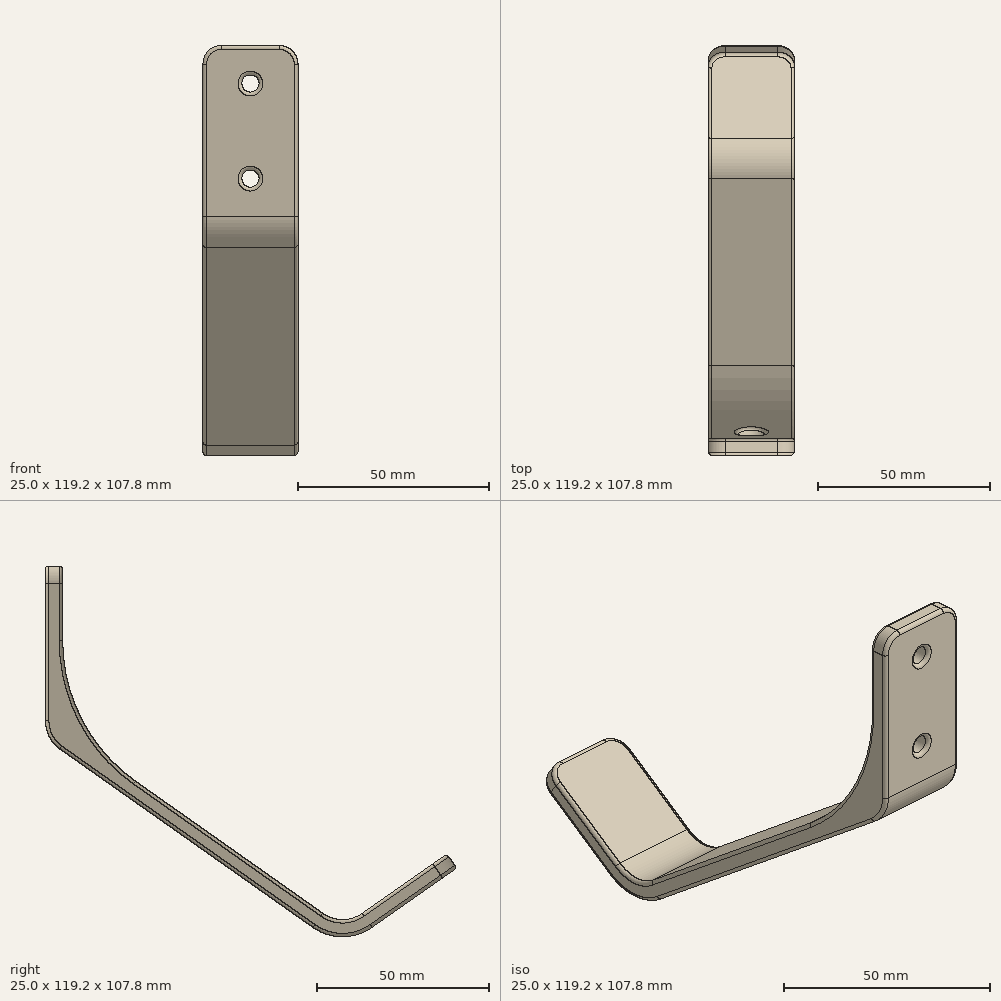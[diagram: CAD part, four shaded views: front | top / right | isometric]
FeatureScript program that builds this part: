
annotation { "Feature Type Name" : "Feature", "Feature Type Description" : "" }
export const myFeature = defineFeature(function(context is Context, id is Id, definition is map)
    precondition{}
    {
        {
            var Q0;
            Q0=qCreatedBy(makeId("Right.planeOp"),FACE);
            var sketch = newSketch(context, id + "F0", { "sketchPlane" : qUnion([Q0])});
            skLineSegment(sketch, "E0", {"start": v(0, 105) * mm, "end": v(0, 60) * mm});
            skLineSegment(sketch, "E1", {"start": v(2.12, 55.91) * mm, "end": v(75.67, 4.05) * mm});
            skLineSegment(sketch, "E2", {"start": v(87.17, 4.03) * mm, "end": v(111.74, 21.24) * mm});
            skPoint(sketch, "E3.visualSharp", {"position": v(81.41, 0) * mm});
            skArc(sketch, "E3.filletArc", {"start": v(75.67, 4.05) * mm, "mid": v(81.42, 2.22) * mm, "end": v(87.17, 4.03) * mm});
            skPoint(sketch, "E4.visualSharp", {"position": v(0, 57.4) * mm});
            skArc(sketch, "E4.filletArc", {"start": v(0, 60) * mm, "mid": v(0.56, 57.7) * mm, "end": v(2.12, 55.91) * mm});
            skLineSegment(sketch, "E5.0", {"start": v(90.04, -0.07) * mm, "end": v(114.61, 17.14) * mm});
            skLineSegment(sketch, "E5.1", {"start": v(-5, 105) * mm, "end": v(-5, 60) * mm});
            skArc(sketch, "E5.2", {"start": v(-5, 60) * mm, "mid": v(-3.88, 55.4) * mm, "end": v(-0.76, 51.83) * mm});
            skLineSegment(sketch, "E5.3", {"start": v(-0.76, 51.83) * mm, "end": v(72.8, -0.04) * mm});
            skArc(sketch, "E5.4", {"start": v(72.8, -0.04) * mm, "mid": v(81.4, -2.78) * mm, "end": v(90.04, -0.07) * mm});
            skLineSegment(sketch, "E6", {"start": v(0, 105) * mm, "end": v(-5, 105) * mm});
            skLineSegment(sketch, "E7", {"start": v(111.74, 21.24) * mm, "end": v(114.61, 17.14) * mm});
            skCircle(sketch, "E8", {"center": v(50, 83.33) * mm, "radius": 50 * mm});
            skSolve(sketch);
        }
        {
            var Q0;
            Q0=makeQuery(id+"F0.imprint","IMPRINT",FACE,{"disambiguationData":[TD([[makeQuery(id+"F0.imprint","IMPRINT",EDGE,{"derivedFrom":sQuery(id+"F0.wireOp",EDGE,"E0")}),-1.0]])]});
            var Q1;
            {var subQ0=sQuery(id+"F0.wireOp",EDGE,"E4.filletArc");Q1=makeQuery(id+"F0.imprint","IMPRINT",FACE,{"disambiguationData":[TD([[makeQuery(id+"F0.imprint","IMPRINT",EDGE,{"derivedFrom":subQ0}),1.0]])]});}
            extrude(context, id + "F1", {"entities" : qUnion([Q0, Q1]), "endBound" : BoundingType.SYMMETRIC, "depth" : 25 * mm});
        }
        {
            var Q0;
            Q0=qCreatedBy(makeId("Front.planeOp"),FACE);
            var sketch = newSketch(context, id + "F2", { "sketchPlane" : qUnion([Q0])});
            skCircle(sketch, "E9", {"center": v(0, 95) * mm, "radius": 2.25 * mm});
            skCircle(sketch, "E10", {"center": v(0, 70) * mm, "radius": 2.25 * mm});
            skCircle(sketch, "E11", {"center": v(0, 70) * mm, "radius": 4 * mm});
            skSolve(sketch);
        }
        {
            var Q0;
            Q0=makeQuery(id+"F2.imprint","IMPRINT",FACE,{"disambiguationData":[TD([[makeQuery(id+"F2.imprint","IMPRINT",EDGE,{"derivedFrom":sQuery(id+"F2.wireOp",EDGE,"E9")}),1.0]])]});
            var Q1;
            Q1=makeQuery(id+"F2.imprint","IMPRINT",FACE,{"disambiguationData":[TD([[makeQuery(id+"F2.imprint","IMPRINT",EDGE,{"derivedFrom":sQuery(id+"F2.wireOp",EDGE,"E10")}),1.0]])]});
            extrude(context, id + "F3", {"entities" : qUnion([Q0, Q1]), "operationType" : NewBodyOperationType.REMOVE, "endBound" : BoundingType.SYMMETRIC, "oppositeDirection" : true, "depth" : 25 * mm});
        }
        {
            var Q0;
            Q0 = qSketchRegion(id + "F2", true);
            extrude(context, id + "F4", {"entities" : qUnion([Q0]), "operationType" : NewBodyOperationType.REMOVE, "oppositeDirection" : true, "depth" : 25 * mm});
        }
        {
            var Q0;
            Q0=makeQuery(id+"F1.opExtrude","CAP_EDGE",EDGE,{"disambiguationData":[OSD([sQuery(id+"F0.wireOp",EDGE,"E6")])],"isStart":false});
            var Q1;
            Q1=makeQuery(id+"F1.opExtrude","CAP_EDGE",EDGE,{"disambiguationData":[OSD([sQuery(id+"F0.wireOp",EDGE,"E6")])],"isStart":true});
            var Q2;
            Q2=makeQuery(id+"F1.opExtrude","CAP_EDGE",EDGE,{"disambiguationData":[OSD([sQuery(id+"F0.wireOp",EDGE,"E7")])],"isStart":false});
            var Q3;
            Q3=makeQuery(id+"F1.opExtrude","CAP_EDGE",EDGE,{"disambiguationData":[OSD([sQuery(id+"F0.wireOp",EDGE,"E7")])],"isStart":true});
            fillet(context, id + "F5", {"entities" : qUnion([Q0, Q1, Q2, Q3]), "radius" : 5 * mm, "tangentPropagation" : true, "allowEdgeOverflow" : false});
        }
        {
            var Q0;
            Q0=makeQuery(id+"F1.opExtrude","SWEPT_FACE",FACE,{"disambiguationData":[OSD([sQuery(id+"F0.wireOp",EDGE,"E1")])]});
            var Q1;
            Q1=makeQuery(id+"F1.opExtrude","SWEPT_FACE",FACE,{"disambiguationData":[OSD([sQuery(id+"F0.wireOp",EDGE,"E5.1")])]});
            var Q2;
            Q2=makeQuery(id+"F3.boolean.opBoolean","INTERSECT",EDGE,{"derivedFrom":[makeQuery(id+"F1.opExtrude","SWEPT_FACE",FACE,{"disambiguationData":[OSD([sQuery(id+"F0.wireOp",EDGE,"E0")])]}),makeQuery(id+"F3.opExtrude","SWEPT_FACE",FACE,{"disambiguationData":[OSD([sQuery(id+"F2.wireOp",EDGE,"E9")])]})]});
            var Q3;
            Q3=makeQuery(id+"F4.boolean.opBoolean","INTERSECT",EDGE,{"derivedFrom":[makeQuery(id+"F1.opExtrude","SWEPT_FACE",FACE,{"disambiguationData":[OSD([sQuery(id+"F0.wireOp",EDGE,"E8")])]}),makeQuery(id+"F4.opExtrude","SWEPT_FACE",FACE,{"disambiguationData":[OSD([sQuery(id+"F2.wireOp",EDGE,"E11")])]})]});
            fillet(context, id + "F6", {"entities" : qUnion([Q0, Q1, Q2, Q3]), "radius" : 1 * mm, "tangentPropagation" : true, "allowEdgeOverflow" : false});
        }
    });
